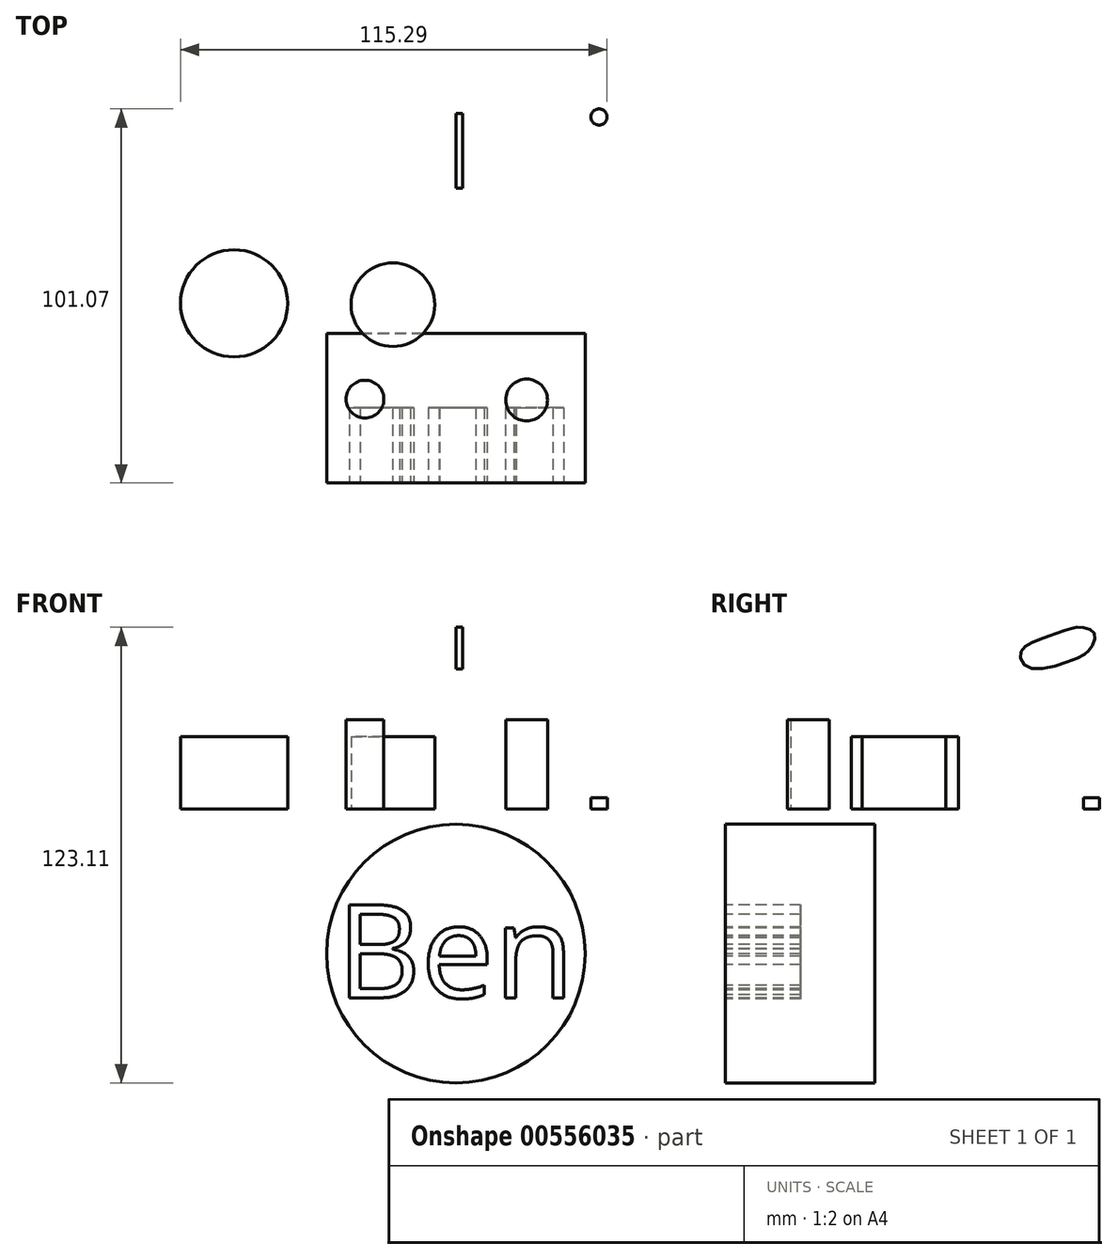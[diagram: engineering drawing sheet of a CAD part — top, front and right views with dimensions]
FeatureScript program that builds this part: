
annotation { "Feature Type Name" : "Feature", "Feature Type Description" : "" }
export const myFeature = defineFeature(function(context is Context, id is Id, definition is map)
    precondition{}
    {
        {
            var Q0;
            Q0=qCreatedBy(makeId("Front.planeOp"),FACE);
            var sketch = newSketch(context, id + "F0", { "sketchPlane" : qUnion([Q0])});
            skCircle(sketch, "E0", {"center": v(0, -39.07) * mm, "radius": 34.93 * mm});
            skSolve(sketch);
        }
        {
            var Q0;
            Q0=makeQuery(id+"F0.imprint","IMPRINT",FACE,{"disambiguationData":[TD([[makeQuery(id+"F0.imprint","IMPRINT",EDGE,{"derivedFrom":sQuery(id+"F0.wireOp",EDGE,"E0")}),1.0]])]});
            extrude(context, id + "F1", {"entities" : qUnion([Q0]), "depth" : 40.4 * mm, "offsetDistance" : 25.4 * mm});
        }
        {
            var Q0;
            Q0=qCreatedBy(makeId("Top.planeOp"),FACE);
            var sketch = newSketch(context, id + "F2", { "sketchPlane" : qUnion([Q0])});
            skCircle(sketch, "E1", {"center": v(19.1, -17.99) * mm, "radius": 5.66 * mm});
            skCircle(sketch, "E2", {"center": v(-24.56, -17.74) * mm, "radius": 5.1 * mm});
            skSolve(sketch);
        }
        {
            var Q0;
            Q0=makeQuery(id+"F2.imprint","IMPRINT",FACE,{"disambiguationData":[TD([[makeQuery(id+"F2.imprint","IMPRINT",EDGE,{"derivedFrom":sQuery(id+"F2.wireOp",EDGE,"E2")}),1.0]])]});
            var Q1;
            Q1=makeQuery(id+"F2.imprint","IMPRINT",FACE,{"disambiguationData":[TD([[makeQuery(id+"F2.imprint","IMPRINT",EDGE,{"derivedFrom":sQuery(id+"F2.wireOp",EDGE,"E1")}),1.0]])]});
            extrude(context, id + "F3", {"entities" : qUnion([Q0, Q1]), "depth" : 24.13 * mm, "offsetDistance" : 25.4 * mm});
        }
        {
            var Q0;
            Q0=qCreatedBy(makeId("Top.planeOp"),FACE);
            var sketch = newSketch(context, id + "F4", { "sketchPlane" : qUnion([Q0])});
            skCircle(sketch, "E3", {"center": v(-59.95, 8.13) * mm, "radius": 14.48 * mm});
            skCircle(sketch, "E4", {"center": v(-17.03, 7.8) * mm, "radius": 11.3 * mm});
            skSolve(sketch);
        }
        {
            var Q0;
            Q0=makeQuery(id+"F4.imprint","IMPRINT",FACE,{"disambiguationData":[TD([[makeQuery(id+"F4.imprint","IMPRINT",EDGE,{"derivedFrom":sQuery(id+"F4.wireOp",EDGE,"E3")}),1.0]])]});
            var Q1;
            Q1=makeQuery(id+"F4.imprint","IMPRINT",FACE,{"disambiguationData":[TD([[makeQuery(id+"F4.imprint","IMPRINT",EDGE,{"derivedFrom":sQuery(id+"F4.wireOp",EDGE,"E4")}),1.0]])]});
            extrude(context, id + "F5", {"entities" : qUnion([Q0, Q1]), "depth" : 19.56 * mm, "offsetDistance" : 25.4 * mm});
        }
        {
            var Q0;
            Q0=makeQuery(id+"F1.opExtrude","CAP_FACE",FACE,{"disambiguationData":[OSD([sQuery(id+"F0.wireOp",EDGE,"E0")])],"isStart":false});
            var sketch = newSketch(context, id + "F6", { "sketchPlane" : qUnion([Q0])});
            skText(sketch, "E5", { "text": "Ben", "fontName": "OpenSans-Regular.ttf"});
            const initialGuessF6  = {"E5": [-0.03226, -0.05102, 1, 0, 0.02534]};
            skSetInitialGuess(sketch, initialGuessF6);
            skSolve(sketch);
        }
        {
            var Q0;
            Q0 = qSketchRegion(id + "F6", true);
            extrude(context, id + "F7", {"entities" : qUnion([Q0]), "operationType" : NewBodyOperationType.REMOVE, "oppositeDirection" : true, "depth" : 20.32 * mm, "offsetDistance" : 25.4 * mm});
        }
        {
            var Q0;
            Q0=qCreatedBy(makeId("Right.planeOp"),FACE);
            var sketch = newSketch(context, id + "F8", { "sketchPlane" : qUnion([Q0])});
            skFitSpline(sketch, "E6", {"points": [v(54.68, 40.8) * mm, v(58.29, 43.56) * mm, v(59.35, 47.37) * mm, v(55.74, 49.07) * mm, v(51.72, 48.43) * mm, v(44.3, 45.67) * mm, v(39.42, 42.5) * mm, v(41.33, 38.26) * mm, v(54.68, 40.8) * mm]});
            skSolve(sketch);
        }
        {
            var Q0;
            Q0 = qSketchRegion(id + "F8", true);
            extrude(context, id + "F9", {"entities" : qUnion([Q0]), "depth" : 1.78 * mm, "offsetDistance" : 25.4 * mm});
        }
        {
            var Q0;
            Q0=qCreatedBy(makeId("Top.planeOp"),FACE);
            var sketch = newSketch(context, id + "F10", { "sketchPlane" : qUnion([Q0])});
            skCircle(sketch, "E7", {"center": v(62.84, 45.36) * mm, "radius": 1.08 * mm});
            skCircle(sketch, "E8", {"center": v(38.68, 58.5) * mm, "radius": 2.18 * mm});
            skSolve(sketch);
        }
        {
            var Q0;
            Q0=makeQuery(id+"F10.imprint","IMPRINT",FACE,{"disambiguationData":[TD([[makeQuery(id+"F10.imprint","IMPRINT",EDGE,{"derivedFrom":sQuery(id+"F10.wireOp",EDGE,"E8")}),1.0]])]});
            extrude(context, id + "F11", {"entities" : qUnion([Q0]), "depth" : 3.05 * mm, "offsetDistance" : 25.4 * mm});
        }
        {
            var Q0;
            Q0=sQuery(id+"F10.wireOp",EDGE,"E7");
            extrude(context, id + "F12", {"bodyType" : ToolBodyType.SURFACE, "surfaceEntities" : qUnion([Q0]), "depth" : 11.18 * mm, "offsetDistance" : 25.4 * mm});
        }
    });
